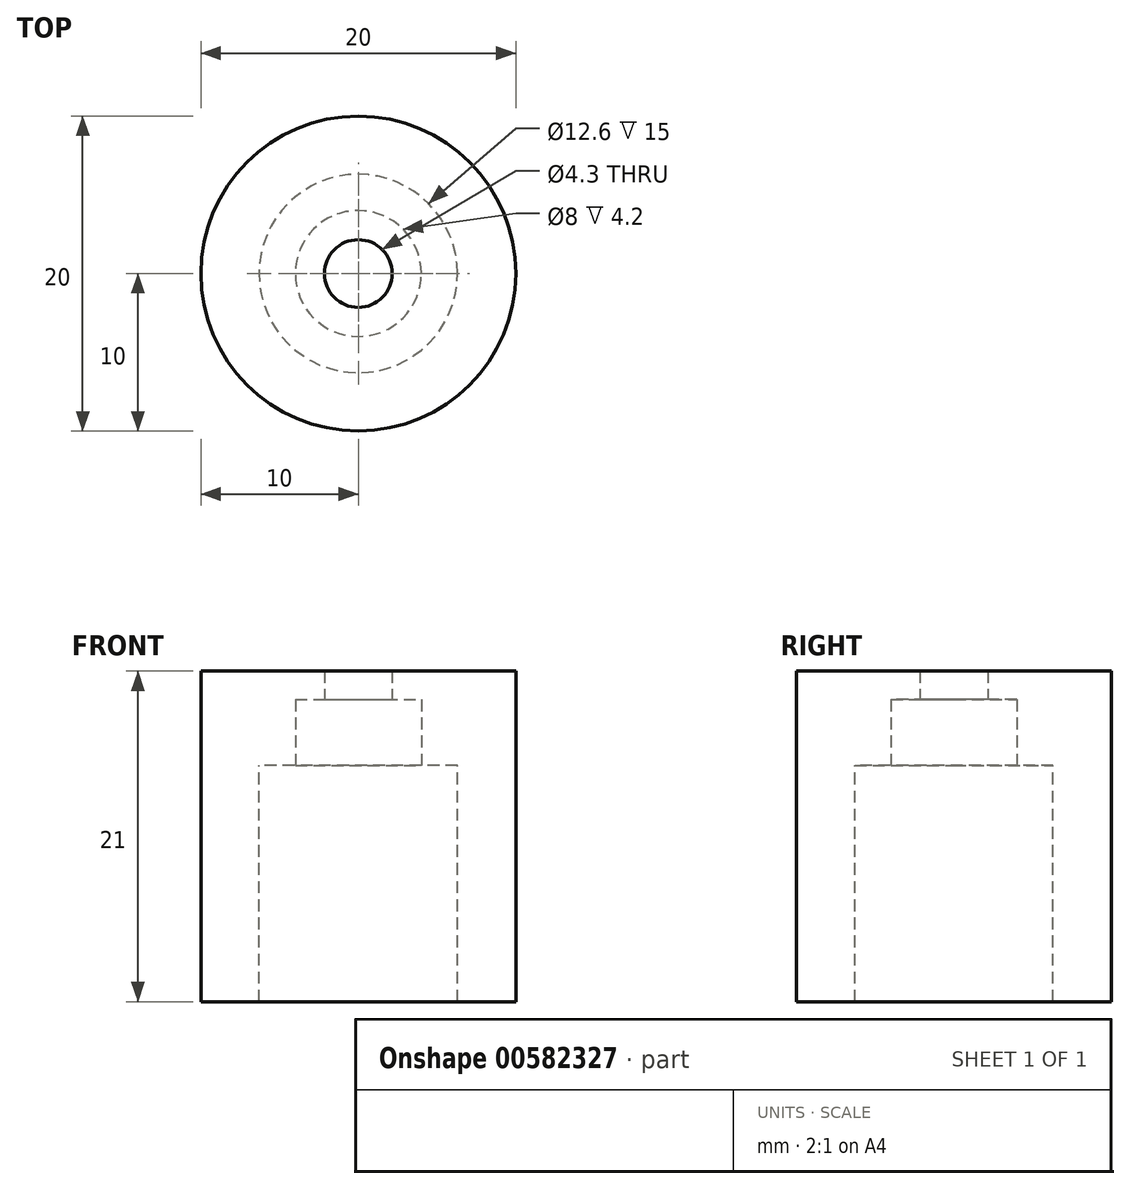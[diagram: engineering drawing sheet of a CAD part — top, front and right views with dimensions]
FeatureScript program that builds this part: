
annotation { "Feature Type Name" : "Feature", "Feature Type Description" : "" }
export const myFeature = defineFeature(function(context is Context, id is Id, definition is map)
    precondition{}
    {
        {
            var Q0;
            Q0=qCreatedBy(makeId("Top.planeOp"),FACE);
            var sketch = newSketch(context, id + "F0", { "sketchPlane" : qUnion([Q0])});
            skCircle(sketch, "E0", {"center": v(0, 0) * mm, "radius": 10 * mm});
            skCircle(sketch, "E1", {"center": v(0, 0) * mm, "radius": 6.3 * mm});
            skSolve(sketch);
        }
        {
            var Q0;
            Q0 = qSketchRegion(id + "F0", true);
            var Q1;
            Q1=makeQuery(id+"F0.imprint","IMPRINT",FACE,{"disambiguationData":[TD([[makeQuery(id+"F0.imprint","IMPRINT",EDGE,{"derivedFrom":sQuery(id+"F0.wireOp",EDGE,"E1")}),1.0]])]});
            extrude(context, id + "F1", {"entities" : qUnion([Q0, Q1]), "depth" : 6 * mm, "offsetDistance" : 25 * mm});
        }
        {
            var Q0;
            Q0=makeQuery(id+"F0.imprint","IMPRINT",FACE,{"disambiguationData":[TD([[makeQuery(id+"F0.imprint","IMPRINT",EDGE,{"derivedFrom":sQuery(id+"F0.wireOp",EDGE,"E0")}),1.0]])]});
            extrude(context, id + "F2", {"entities" : qUnion([Q0]), "operationType" : NewBodyOperationType.ADD, "oppositeDirection" : true, "depth" : 15 * mm, "offsetDistance" : 25 * mm});
        }
        {
            var Q0;
            Q0=makeQuery(id+"F1.opExtrude","CAP_FACE",FACE,{"disambiguationData":[OSD([sQuery(id+"F0.wireOp",EDGE,"E0")])],"isStart":false});
            cPlane(context, id + "F3", {"entities" : qUnion([Q0]), "cplaneType" : CPlaneType.OFFSET, "offset" : 10 * mm, "width" : 150 * mm, "height" : 150 * mm});
        }
        {
            var Q0;
            Q0=qCreatedBy(id+"F3.planeOp",FACE);
            var sketch = newSketch(context, id + "F4", { "sketchPlane" : qUnion([Q0])});
            skCircle(sketch, "E2", {"center": v(0, 0) * mm, "radius": 1 * mm});
            skSolve(sketch);
        }
        {
            var Q0;
            Q0=makeQuery(id+"F4.imprint","IMPRINT",FACE,{"disambiguationData":[TD([[makeQuery(id+"F4.imprint","IMPRINT",EDGE,{"derivedFrom":sQuery(id+"F4.wireOp",EDGE,"E2")}),1.0]])]});
            var Q1;
            Q1=makeQuery(id+"F1.opExtrude","CAP_FACE",FACE,{"disambiguationData":[OSD([sQuery(id+"F0.wireOp",EDGE,"E0")])],"isStart":false});
            var Q2;
            {var subQ0=sQuery(id+"F0.wireOp",EDGE,"E0");Q2=makeQuery(id+"F6.imprint","IMPRINT",FACE,{"disambiguationData":[TD([[makeQuery(id+"F6.imprint","IMPRINT",EDGE,{"derivedFrom":makeQuery(id+"F1.opExtrude","CAP_EDGE",EDGE,{"disambiguationData":[OSD([subQ0])],"isStart":false})}),1.0]])]});}
            var Q3;
            Q3=sQuery(id+"F4.wireOp",EDGE,"E2");
            loft(context, id + "F5", {"sheetProfilesArray" : [{ "sheetProfileEntities" : qUnion([Q0]) }, { "sheetProfileEntities" : qUnion([Q1]) }], "wireProfilesArray" : [{ "wireProfileEntities" : qUnion([Q2]) }, { "wireProfileEntities" : qUnion([Q3]) }]});
        }
        {
            var Q0;
            Q0=makeQuery(id+"F1.opExtrude","CAP_FACE",FACE,{"disambiguationData":[OSD([sQuery(id+"F0.wireOp",EDGE,"E0")])],"isStart":false});
            var sketch = newSketch(context, id + "F6", { "sketchPlane" : qUnion([Q0])});
            skSolve(sketch);
        }
        {
            var Q0;
            Q0=sQuery(id+"F0.wireOp",VERTEX,"E0.center");
            var Q1;
            Q1=makeQuery(id+"F1.opExtrude","SWEPT_BODY",BODY,{"disambiguationData":[OSD([sQuery(id+"F0.wireOp",EDGE,"E0")])]});
            hole(context, id + "F7", {"style" : HoleStyle.C_BORE, "endStyle" : HoleEndStyle.THROUGH, "oppositeDirection" : true, "holeDiameter" : 4.3 * mm, "cBoreDiameter" : 8 * mm, "cBoreDepth" : 4.2 * mm, "majorDiameter" : 5 * mm, "isTappedThrough" : true, "tappedDepth" : 12 * mm, "tapClearance" : 3, "locations" : qUnion([Q0]), "scope" : qUnion([Q1])});
        }
        {
            var Q0;
            Q0=sQuery(id+"F0.wireOp",VERTEX,"E0.center");
            var Q1;
            Q1=makeQuery(id+"F5.opLoft","SWEPT_BODY",BODY,{"disambiguationData":[OSD([sQuery(id+"F0.wireOp",EDGE,"E0"),makeQuery(id+"F4.imprint","IMPRINT",FACE,{"disambiguationData":[TD([[makeQuery(id+"F4.imprint","IMPRINT",EDGE,{"derivedFrom":sQuery(id+"F4.wireOp",EDGE,"E2")}),1.0]])]})])]});
            hole(context, id + "F8", {"style" : HoleStyle.SIMPLE, "endStyle" : HoleEndStyle.BLIND, "oppositeDirection" : true, "holeDiameter" : 3.2 * mm, "majorDiameter" : 5 * mm, "holeDepth" : 8 * mm, "isTappedThrough" : true, "tappedDepth" : 12 * mm, "tapClearance" : 3, "locations" : qUnion([Q0]), "scope" : qUnion([Q1])});
        }
        {
            var Q0;
            Q0=makeQuery(id+"F5.opLoft","SWEPT_BODY",BODY,{"disambiguationData":[OSD([sQuery(id+"F0.wireOp",EDGE,"E0"),makeQuery(id+"F4.imprint","IMPRINT",FACE,{"disambiguationData":[TD([[makeQuery(id+"F4.imprint","IMPRINT",EDGE,{"derivedFrom":sQuery(id+"F4.wireOp",EDGE,"E2")}),1.0]])]})])]});
            deleteBodies(context, id + "F9", {"entities" : qUnion([Q0])});
        }
    });
